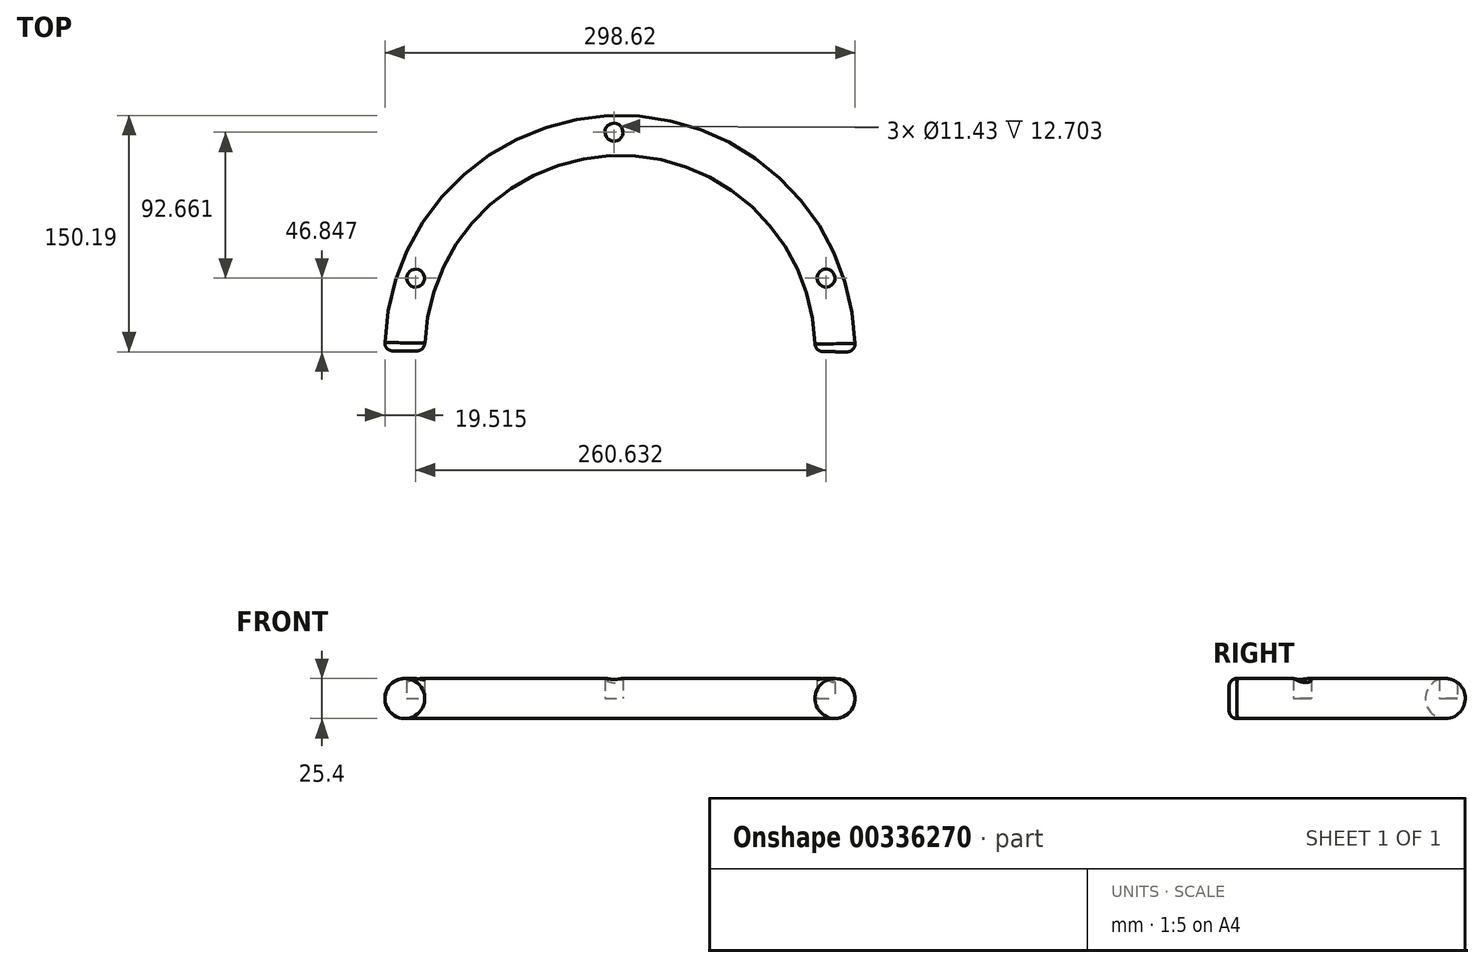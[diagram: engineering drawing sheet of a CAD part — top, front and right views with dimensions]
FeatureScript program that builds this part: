
annotation { "Feature Type Name" : "Feature", "Feature Type Description" : "" }
export const myFeature = defineFeature(function(context is Context, id is Id, definition is map)
    precondition{}
    {
        {
            var Q0;
            Q0=qCreatedBy(makeId("Top.planeOp"),FACE);
            var sketch = newSketch(context, id + "F0", { "sketchPlane" : qUnion([Q0])});
            skArc(sketch, "E0", {"start": v(0, 0) * mm, "mid": v(-50.8, 50.97) * mm, "end": v(-101.6, 0) * mm});
            skSolve(sketch);
        }
        {
            var Q0;
            Q0=qCreatedBy(makeId("Front.planeOp"),FACE);
            var sketch = newSketch(context, id + "F1", { "sketchPlane" : qUnion([Q0])});
            skCircle(sketch, "E1", {"center": v(-187.49, 0) * mm, "radius": 12.7 * mm});
            skSolve(sketch);
        }
        {
            var Q0;
            Q0=makeQuery(id+"F1.imprint","IMPRINT",FACE,{"disambiguationData":[TD([[makeQuery(id+"F1.imprint","IMPRINT",EDGE,{"derivedFrom":sQuery(id+"F1.wireOp",EDGE,"E1")}),1.0]])]});
            var Q1;
            Q1=sQuery(id+"F0.wireOp",EDGE,"E0");
            sweep(context, id + "F2", {"profiles" : qUnion([Q0]), "path" : qUnion([Q1])});
        }
        {
            var Q0;
            Q0=makeQuery(id+"F2.opSweep","SWEPT_FACE",FACE,{"disambiguationData":[OSD([sQuery(id+"F0.wireOp",EDGE,"E0"),sQuery(id+"F1.wireOp",EDGE,"E1")])]});
            fillet(context, id + "F3", {"entities" : qUnion([Q0]), "radius" : 5.08 * mm, "tangentPropagation" : true, "allowEdgeOverflow" : false});
        }
        {
            var Q0;
            Q0=qCreatedBy(makeId("Top.planeOp"),FACE);
            var sketch = newSketch(context, id + "F4", { "sketchPlane" : qUnion([Q0])});
            skPoint(sketch, "E2", {"position": v(-180.59, 46.22) * mm});
            skPoint(sketch, "E3", {"position": v(-54.6, 46.22) * mm});
            skPoint(sketch, "E4", {"position": v(-54.6, 138.88) * mm});
            skPoint(sketch, "E5", {"position": v(80.05, 46.22) * mm});
            skSolve(sketch);
        }
        {
            var Q0;
            Q0=sQuery(id+"F4.wireOp",VERTEX,"E2");
            var Q1;
            Q1=sQuery(id+"F4.wireOp",VERTEX,"E4");
            var Q2;
            Q2=sQuery(id+"F4.wireOp",VERTEX,"E5");
            var Q3;
            Q3=makeQuery(id+"F2.opSweep","SWEPT_BODY",BODY,{"disambiguationData":[OSD([sQuery(id+"F0.wireOp",EDGE,"E0"),sQuery(id+"F1.wireOp",EDGE,"E1")])]});
            hole(context, id + "F5", {"style" : HoleStyle.C_BORE, "endStyle" : HoleEndStyle.BLIND, "oppositeDirection" : true, "holeDiameter" : 11.43 * mm, "cBoreDiameter" : 11.43 * mm, "cBoreDepth" : 5 * mm, "holeDepth" : 25.4 * mm, "tappedDepth" : 101.6 * mm, "tapClearance" : 3, "locations" : qUnion([Q0, Q1, Q2]), "scope" : qUnion([Q3])});
        }
    });
